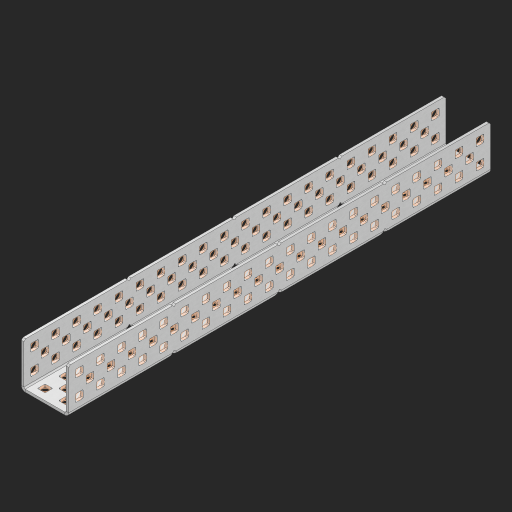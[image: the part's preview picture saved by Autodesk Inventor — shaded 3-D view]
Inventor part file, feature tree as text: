
AUTODESK INVENTOR PART (.ipt)
format: ipt  version: 2023 (Build 270158000, 158)  size: 2,158,080 bytes
history: native  units: in
note: dims shown in document units (in); Inventor stores cm internally (conversion verified against a paired STEP export)
features: other x263, extrude x234, sheet_metal_op x8, sketch x7, mirror x3, pattern_linear x2, chamfer x1
ambient origin geometry x8: Origin, YZ Plane, XZ Plane, XY Plane, X Axis, Y Axis, Z Axis, Center Point
bodies: Solid1 (feature_tree), Body (feature_tree)
feature tree (518):
  other  "Table"
  other  "Alu C 1x2x1x20"
  other  "Alu C 1x2x1x19"
  other  "Alu C 1x2x1x18"
  other  "Alu C 1x2x1x17"
  other  "Alu C 1x2x1x16"
  other  "Alu C 1x2x1x15"
  other  "Alu C 1x2x1x14"
  other  "Alu C 1x2x1x13"
  other  "Alu C 1x2x1x12"
  other  "Alu C 1x2x1x11"
  other  "Alu C 1x2x1x10"
  other  "Alu C 1x2x1x9"
  other  "Alu C 1x2x1x8"
  other  "Alu C 1x2x1x7"
  other  "Alu C 1x2x1x6"
  other  "Alu C 1x2x1x5"
  other  "Alu C 1x2x1x4"
  other  "Alu C 1x2x1x3"
  other  "Alu C 1x2x1x2"
  other  "Alu C 1x2x1x1"
  sheet_metal_op  "Flanges"
  sheet_metal_op  "Body Pattern"
  pattern_linear  "Center Pattern"  Spacing1=1.0in  [1 undecoded]
  other  "Arc Length"
  mirror  "Notch Mirror"
  pattern_linear  "Notch Pattern"  Spacing1=0.25in  [1 undecoded]
  other  "Diagonal Plane"
  mirror  "Flange 1"
  mirror  "Flange 2"
  chamfer  "End Chamfer"
  sketch  "Sketch1"  dims[d0=1.0in]
  other  "Plate1"
  sketch  "Sketch2"  dims[d1=10.0in]
  other  "Plate2"
  sheet_metal_op  "Bend1"
  sheet_metal_op  "Corner1"
  sketch  "Sketch8"  dims[d2=0.0625in]
  sketch  "Sketch9"  dims[d3=0.0625in]
  other  "Srf91"
  sheet_metal_op  "Body Pattern Sketch"
  other  "Srf92"
  sketch  "Sketch13"  dims[d4=0.0312in]
  sketch  "Sketch15"  dims[d5=0.125in]
  sketch  "Sketch16"  dims[d6=0.0625in d7=1.0in d8=90.0deg d9=0.0312in d10=0.25in d11=0.0625in d12=0.0625in d49=0.182in d50=0.02in d52=0.25in d53=0.0625in d54=0.0in d55=0.172in d56=1.0in d57=0.0in d60=7.874in d62=0.5in d63=0.7874in d65=0.5in d85=0.1473in d86=0.1782in d88=0.04in d89=0.0625in d90=0.0in d91=0.04in d92=0.0491in d95=2.5in d96=0.04in d97=0.25in d98=45.0deg d99=0.25in d102=2.497in d106=0.182in d107=0.02in d108=0.5in d110=0.0625in d111=0.0in d112=0.172in d113=0.5in d114=0.0in d117=0.5in d118=0.5in d131=0.25in d132=0.25in]
  other  "Srf786"
  other  "Srf889"
  other  "Srf890"
  other  "Srf891"
  other  "Srf892"
  other  "Srf893"
  other  "Srf894"
  other  "Srf895"
  other  "Srf896"
  other  "Srf996"
  other  "Srf997"
  other  "Srf998"
  other  "Srf999"
  other  "Srf1000"
  other  "Srf1255"
  other  "Srf1256"
  other  "Srf1257"
  other  "Srf1258"
  other  "Srf1259"
  other  "Srf1315"
  other  "Srf1316"
  other  "Srf1317"
  other  "Srf1325"
  other  "Srf1326"
  other  "Srf1327"
  other  "Srf1328"
  other  "Srf1329"
  other  "Srf1330"
  other  "Srf1331"
  other  "Srf1332"
  other  "Srf1338"
  other  "Srf1339"
  other  "Srf1340"
  other  "Srf1341"
  other  "Srf1342"
  other  "Srf1369"
  other  "Srf1370"
  other  "Srf1371"
  other  "Srf1372"
  other  "Srf1373"
  other  "Srf1374"
  other  "Srf1375"
  other  "Srf1376"
  other  "Srf1384"
  other  "Srf1385"
  other  "Srf1386"
  other  "Srf1387"
  other  "Srf1388"
  other  "Srf1389"
  other  "Srf1390"
  other  "Srf1391"
  other  "Srf1397"
  other  "Srf1398"
  other  "Srf1399"
  other  "Srf1400"
  other  "Srf1401"
  other  "Srf1428"
  other  "Srf1429"
  other  "Srf1430"
  other  "Srf1431"
  other  "Srf1432"
  other  "Srf1433"
  other  "Srf1434"
  other  "Srf1473"
  other  "Srf1474"
  other  "Srf1475"
  other  "Srf1476"
  other  "Srf1477"
  other  "Srf1478"
  other  "Srf1479"
  other  "Srf1480"
  other  "Srf1481"
  other  "Srf1482"
  other  "Srf1483"
  other  "Srf1484"
  other  "Srf1485"
  other  "Srf1486"
  other  "Srf1487"
  other  "Srf1488"
  other  "Srf1489"
  other  "Srf1490"
  other  "Srf1491"
  other  "Srf1500"
  other  "Srf1501"
  other  "Srf1502"
  other  "Srf1503"
  other  "Srf1504"
  other  "Srf1505"
  other  "Srf1506"
  other  "Srf1507"
  other  "Srf1508"
  other  "Srf1509"
  other  "Srf1510"
  other  "Srf1511"
  other  "Srf1512"
  other  "Srf1513"
  other  "Srf1514"
  other  "Srf1515"
  other  "Srf1516"
  other  "Srf1517"
  other  "Srf1518"
  other  "Srf1519"
  other  "Srf1520"
  other  "Srf1521"
  other  "Srf1522"
  other  "Srf1523"
  other  "Srf1524"
  other  "Srf1525"
  other  "Srf1526"
  other  "Srf1527"
  other  "Srf1528"
  other  "Srf1529"
  other  "Srf1530"
  other  "Srf1531"
  other  "Srf1532"
  other  "Srf1533"
  other  "Srf1534"
  other  "Srf1535"
  other  "Srf1536"
  other  "Srf1537"
  other  "Srf1538"
  other  "Srf1539"
  other  "Srf1540"
  other  "Srf1541"
  other  "Srf1542"
  other  "Srf1543"
  other  "Srf1544"
  other  "Srf1545"
  other  "Srf1546"
  other  "Srf1547"
  other  "Srf1548"
  other  "Srf1549"
  other  "Srf1550"
  other  "Srf1551"
  other  "Srf1552"
  other  "Srf1553"
  other  "Srf1554"
  other  "Srf1555"
  other  "Srf1556"
  other  "Srf1557"
  other  "Srf1558"
  other  "Srf1559"
  other  "Srf1560"
  other  "Srf1561"
  other  "Srf1562"
  other  "Srf1563"
  other  "Srf1564"
  other  "Srf1565"
  other  "Srf1566"
  other  "Srf1567"
  other  "Srf1568"
  other  "Srf1569"
  other  "Srf1570"
  other  "Srf1571"
  other  "Srf1572"
  other  "Srf1573"
  other  "Srf1574"
  other  "Srf1575"
  other  "Srf1576"
  other  "Srf1577"
  other  "Srf1578"
  other  "Srf1579"
  other  "Srf1580"
  other  "Srf1581"
  other  "Srf1582"
  other  "Srf1583"
  other  "Srf1584"
  other  "Srf1585"
  other  "Srf1586"
  other  "Srf1587"
  other  "Srf1588"
  other  "Srf1589"
  other  "Srf1590"
  other  "Srf1591"
  other  "Srf1592"
  other  "Srf1593"
  other  "Srf1594"
  other  "Srf1595"
  other  "Srf1596"
  other  "Srf1597"
  other  "Srf1598"
  other  "Srf1599"
  other  "Srf1600"
  other  "Srf1601"
  other  "Srf1602"
  other  "Srf1603"
  other  "Srf1604"
  other  "Srf1605"
  other  "Srf1606"
  other  "Srf1607"
  other  "Srf1608"
  other  "Srf1609"
  other  "Srf1610"
  other  "Srf1611"
  other  "Srf1612"
  other  "Srf1613"
  other  "Srf1614"
  other  "Srf1615"
  other  "Srf1616"
  other  "Srf1617"
  other  "Srf1618"
  other  "Srf1619"
  other  "Srf1620"
  other  "Srf1621"
  other  "Srf1622"
  other  "Srf1623"
  other  "Srf1624"
  other  "Srf1625"
  other  "Srf1626"
  other  "Srf1627"
  other  "Srf1628"
  other  "Srf1629"
  other  "Srf1630"
  other  "Srf1631"
  other  "Srf1632"
  other  "Srf1633"
  other  "Srf1634"
  other  "Srf1635"
  other  "Srf1636"
  other  "Srf1637"
  other  "Srf1638"
  other  "Srf1639"
  other  "Srf1640"
  other  "Srf1641"
  other  "Srf1642"
  other  "Srf1643"
  other  "Srf1644"
  other  "Srf1645"
  other  "Srf1646"
  other  "Srf1647"
  other  "Srf1648"
  other  "Srf1649"
  other  "Srf1650"
  other  "Srf1651"
  sheet_metal_op  "Body Stamp"
  sheet_metal_op  "Body Circle"
  other  "Center Stamp"
  other  "Center Circle"
  sheet_metal_op  "Notch"
  extrude  "ExtrusionSrf92"  Depth=0.0625in
  extrude  "ExtrusionSrf889"  Depth=0.0625in
  extrude  "ExtrusionSrf890"  Depth=0.5in
  extrude  "ExtrusionSrf891"  Depth=0.02in
  extrude  "ExtrusionSrf892"  Depth=0.5in
  extrude  "ExtrusionSrf893"  Depth=0.0625in
  extrude  "ExtrusionSrf894"  TaperAngle=0.0deg  [1 undecoded]
  extrude  "ExtrusionSrf895"  Depth=0.5in
  extrude  "ExtrusionSrf896"  Depth=1.0in TaperAngle=0.0deg
  extrude  "ExtrusionSrf996"  Depth=0.5in
  extrude  "ExtrusionSrf997"  Depth=0.5in
  extrude  "ExtrusionSrf998"  Depth=0.5in
  extrude  "ExtrusionSrf999"  Depth=0.5in
  extrude  "ExtrusionSrf1000"  Depth=0.5in
  extrude  "ExtrusionSrf1255"  Depth=0.0625in
  extrude  "ExtrusionSrf1256"  TaperAngle=0.0deg  [1 undecoded]
  extrude  "ExtrusionSrf1257"  Depth=0.5in
  extrude  "ExtrusionSrf1258"  Depth=0.5in
  extrude  "ExtrusionSrf1259"  Depth=2.5in
  extrude  "ExtrusionSrf1315"  Depth=0.5in TaperAngle=45.0deg
  extrude  "ExtrusionSrf1316"  Depth=0.5in
  extrude  "ExtrusionSrf1355"  Depth=0.5in
  extrude  "ExtrusionSrf1356"  Depth=0.5in
  extrude  "ExtrusionSrf1357"  Depth=0.02in
  extrude  "ExtrusionSrf1358"  Depth=0.5in
  extrude  "ExtrusionSrf1359"  Depth=0.0625in
  extrude  "ExtrusionSrf1360"  TaperAngle=0.0deg  [1 undecoded]
  extrude  "ExtrusionSrf1361"  Depth=0.5in
  extrude  "ExtrusionSrf1362"  Depth=0.5in TaperAngle=0.0deg
  extrude  "ExtrusionSrf1363"  Depth=0.5in
  extrude  "ExtrusionSrf1364"  Depth=0.5in
  extrude  "ExtrusionSrf1365"  Depth=0.5in
  extrude  "ExtrusionSrf1366"  Depth=0.5in
  extrude  "ExtrusionSrf1367"  [1 undecoded]
  extrude  "ExtrusionSrf1368"  [1 undecoded]
  extrude  "ExtrusionSrf1369"  [1 undecoded]
  extrude  "ExtrusionSrf1370"  [1 undecoded]
  extrude  "ExtrusionSrf1371"  [1 undecoded]
  extrude  "ExtrusionSrf1372"  [1 undecoded]
  extrude  "ExtrusionSrf1373"  [1 undecoded]
  extrude  "ExtrusionSrf1374"  [1 undecoded]
  extrude  "ExtrusionSrf1375"  [1 undecoded]
  extrude  "ExtrusionSrf1414"  [1 undecoded]
  extrude  "ExtrusionSrf1415"  [1 undecoded]
  extrude  "ExtrusionSrf1416"  [1 undecoded]
  extrude  "ExtrusionSrf1417"  [1 undecoded]
  extrude  "ExtrusionSrf1418"  [1 undecoded]
  extrude  "ExtrusionSrf1419"  [1 undecoded]
  extrude  "ExtrusionSrf1420"  [1 undecoded]
  extrude  "ExtrusionSrf1421"  [1 undecoded]
  extrude  "ExtrusionSrf1422"  [1 undecoded]
  extrude  "ExtrusionSrf1423"  [1 undecoded]
  extrude  "ExtrusionSrf1424"  [1 undecoded]
  extrude  "ExtrusionSrf1425"  [1 undecoded]
  extrude  "ExtrusionSrf1426"  [1 undecoded]
  extrude  "ExtrusionSrf1427"  [1 undecoded]
  extrude  "ExtrusionSrf1428"  [1 undecoded]
  extrude  "ExtrusionSrf1429"  [1 undecoded]
  extrude  "ExtrusionSrf1430"  [1 undecoded]
  extrude  "ExtrusionSrf1431"  [1 undecoded]
  extrude  "ExtrusionSrf1432"  [1 undecoded]
  extrude  "ExtrusionSrf1433"  [1 undecoded]
  extrude  "ExtrusionSrf1434"  [1 undecoded]
  extrude  "ExtrusionSrf1473"  [1 undecoded]
  extrude  "ExtrusionSrf1474"  [1 undecoded]
  extrude  "ExtrusionSrf1475"  [1 undecoded]
  extrude  "ExtrusionSrf1476"  [1 undecoded]
  extrude  "ExtrusionSrf1477"  [1 undecoded]
  extrude  "ExtrusionSrf1478"  [1 undecoded]
  extrude  "ExtrusionSrf1479"  [1 undecoded]
  extrude  "ExtrusionSrf1480"  [1 undecoded]
  extrude  "ExtrusionSrf1481"  [1 undecoded]
  extrude  "ExtrusionSrf1482"  [1 undecoded]
  extrude  "ExtrusionSrf1483"  [1 undecoded]
  extrude  "ExtrusionSrf1484"  [1 undecoded]
  extrude  "ExtrusionSrf1485"  [1 undecoded]
  extrude  "ExtrusionSrf1486"  [1 undecoded]
  extrude  "ExtrusionSrf1487"  [1 undecoded]
  extrude  "ExtrusionSrf1488"  [1 undecoded]
  extrude  "ExtrusionSrf1489"  [1 undecoded]
  extrude  "ExtrusionSrf1490"  [1 undecoded]
  extrude  "ExtrusionSrf1491"  [1 undecoded]
  extrude  "ExtrusionSrf1500"  [1 undecoded]
  extrude  "ExtrusionSrf1501"  [1 undecoded]
  extrude  "ExtrusionSrf1502"  [1 undecoded]
  extrude  "ExtrusionSrf1503"  [1 undecoded]
  extrude  "ExtrusionSrf1504"  [1 undecoded]
  extrude  "ExtrusionSrf1505"  [1 undecoded]
  extrude  "ExtrusionSrf1506"  [1 undecoded]
  extrude  "ExtrusionSrf1507"  [1 undecoded]
  extrude  "ExtrusionSrf1508"  [1 undecoded]
  extrude  "ExtrusionSrf1509"  [1 undecoded]
  extrude  "ExtrusionSrf1510"  [1 undecoded]
  extrude  "ExtrusionSrf1511"  [1 undecoded]
  extrude  "ExtrusionSrf1512"  [1 undecoded]
  extrude  "ExtrusionSrf1513"  [1 undecoded]
  extrude  "ExtrusionSrf1514"  [1 undecoded]
  extrude  "ExtrusionSrf1515"  [1 undecoded]
  extrude  "ExtrusionSrf1516"  [1 undecoded]
  extrude  "ExtrusionSrf1517"  [1 undecoded]
  extrude  "ExtrusionSrf1518"  [1 undecoded]
  extrude  "ExtrusionSrf1519"  [1 undecoded]
  extrude  "ExtrusionSrf1520"  [1 undecoded]
  extrude  "ExtrusionSrf1521"  [1 undecoded]
  extrude  "ExtrusionSrf1522"  [1 undecoded]
  extrude  "ExtrusionSrf1523"  [1 undecoded]
  extrude  "ExtrusionSrf1524"  [1 undecoded]
  extrude  "ExtrusionSrf1525"  [1 undecoded]
  extrude  "ExtrusionSrf1526"  [1 undecoded]
  extrude  "ExtrusionSrf1527"  [1 undecoded]
  extrude  "ExtrusionSrf1528"  [1 undecoded]
  extrude  "ExtrusionSrf1529"  [1 undecoded]
  extrude  "ExtrusionSrf1530"  [1 undecoded]
  extrude  "ExtrusionSrf1531"  [1 undecoded]
  extrude  "ExtrusionSrf1532"  [1 undecoded]
  extrude  "ExtrusionSrf1533"  [1 undecoded]
  extrude  "ExtrusionSrf1534"  [1 undecoded]
  extrude  "ExtrusionSrf1535"  [1 undecoded]
  extrude  "ExtrusionSrf1536"  [1 undecoded]
  extrude  "ExtrusionSrf1537"  [1 undecoded]
  extrude  "ExtrusionSrf1538"  [1 undecoded]
  extrude  "ExtrusionSrf1539"  [1 undecoded]
  extrude  "ExtrusionSrf1540"  [1 undecoded]
  extrude  "ExtrusionSrf1541"  [1 undecoded]
  extrude  "ExtrusionSrf1542"  [1 undecoded]
  extrude  "ExtrusionSrf1543"  [1 undecoded]
  extrude  "ExtrusionSrf1544"  [1 undecoded]
  extrude  "ExtrusionSrf1545"  [1 undecoded]
  extrude  "ExtrusionSrf1546"  [1 undecoded]
  extrude  "ExtrusionSrf1547"  [1 undecoded]
  extrude  "ExtrusionSrf1548"  [1 undecoded]
  extrude  "ExtrusionSrf1549"  [1 undecoded]
  extrude  "ExtrusionSrf1550"  [1 undecoded]
  extrude  "ExtrusionSrf1551"  [1 undecoded]
  extrude  "ExtrusionSrf1552"  [1 undecoded]
  extrude  "ExtrusionSrf1553"  [1 undecoded]
  extrude  "ExtrusionSrf1554"  [1 undecoded]
  extrude  "ExtrusionSrf1555"  [1 undecoded]
  extrude  "ExtrusionSrf1556"  [1 undecoded]
  extrude  "ExtrusionSrf1557"  [1 undecoded]
  extrude  "ExtrusionSrf1558"  [1 undecoded]
  extrude  "ExtrusionSrf1559"  [1 undecoded]
  extrude  "ExtrusionSrf1560"  [1 undecoded]
  extrude  "ExtrusionSrf1561"  [1 undecoded]
  extrude  "ExtrusionSrf1562"  [1 undecoded]
  extrude  "ExtrusionSrf1563"  [1 undecoded]
  extrude  "ExtrusionSrf1564"  [1 undecoded]
  extrude  "ExtrusionSrf1565"  [1 undecoded]
  extrude  "ExtrusionSrf1566"  [1 undecoded]
  extrude  "ExtrusionSrf1567"  [1 undecoded]
  extrude  "ExtrusionSrf1568"  [1 undecoded]
  extrude  "ExtrusionSrf1569"  [1 undecoded]
  extrude  "ExtrusionSrf1570"  [1 undecoded]
  extrude  "ExtrusionSrf1571"  [1 undecoded]
  extrude  "ExtrusionSrf1572"  [1 undecoded]
  extrude  "ExtrusionSrf1573"  [1 undecoded]
  extrude  "ExtrusionSrf1574"  [1 undecoded]
  extrude  "ExtrusionSrf1575"  [1 undecoded]
  extrude  "ExtrusionSrf1576"  [1 undecoded]
  extrude  "ExtrusionSrf1577"  [1 undecoded]
  extrude  "ExtrusionSrf1578"  [1 undecoded]
  extrude  "ExtrusionSrf1579"  [1 undecoded]
  extrude  "ExtrusionSrf1580"  [1 undecoded]
  extrude  "ExtrusionSrf1581"  [1 undecoded]
  extrude  "ExtrusionSrf1582"  [1 undecoded]
  extrude  "ExtrusionSrf1583"  [1 undecoded]
  extrude  "ExtrusionSrf1584"  [1 undecoded]
  extrude  "ExtrusionSrf1585"  [1 undecoded]
  extrude  "ExtrusionSrf1586"  [1 undecoded]
  extrude  "ExtrusionSrf1587"  [1 undecoded]
  extrude  "ExtrusionSrf1588"  [1 undecoded]
  extrude  "ExtrusionSrf1589"  [1 undecoded]
  extrude  "ExtrusionSrf1590"  [1 undecoded]
  extrude  "ExtrusionSrf1591"  [1 undecoded]
  extrude  "ExtrusionSrf1592"  [1 undecoded]
  extrude  "ExtrusionSrf1593"  [1 undecoded]
  extrude  "ExtrusionSrf1594"  [1 undecoded]
  extrude  "ExtrusionSrf1595"  [1 undecoded]
  extrude  "ExtrusionSrf1596"  [1 undecoded]
  extrude  "ExtrusionSrf1597"  [1 undecoded]
  extrude  "ExtrusionSrf1598"  [1 undecoded]
  extrude  "ExtrusionSrf1599"  [1 undecoded]
  extrude  "ExtrusionSrf1600"  [1 undecoded]
  extrude  "ExtrusionSrf1601"  [1 undecoded]
  extrude  "ExtrusionSrf1602"  [1 undecoded]
  extrude  "ExtrusionSrf1603"  [1 undecoded]
  extrude  "ExtrusionSrf1604"  [1 undecoded]
  extrude  "ExtrusionSrf1605"  [1 undecoded]
  extrude  "ExtrusionSrf1606"  [1 undecoded]
  extrude  "ExtrusionSrf1607"  [1 undecoded]
  extrude  "ExtrusionSrf1608"  [1 undecoded]
  extrude  "ExtrusionSrf1609"  [1 undecoded]
  extrude  "ExtrusionSrf1610"  [1 undecoded]
  extrude  "ExtrusionSrf1611"  [1 undecoded]
  extrude  "ExtrusionSrf1612"  [1 undecoded]
  extrude  "ExtrusionSrf1613"  [1 undecoded]
  extrude  "ExtrusionSrf1614"  [1 undecoded]
  extrude  "ExtrusionSrf1615"  [1 undecoded]
  extrude  "ExtrusionSrf1616"  [1 undecoded]
  extrude  "ExtrusionSrf1617"  [1 undecoded]
  extrude  "ExtrusionSrf1618"  [1 undecoded]
  extrude  "ExtrusionSrf1619"  [1 undecoded]
  extrude  "ExtrusionSrf1620"  [1 undecoded]
  extrude  "ExtrusionSrf1621"  [1 undecoded]
  extrude  "ExtrusionSrf1622"  [1 undecoded]
  extrude  "ExtrusionSrf1623"  [1 undecoded]
  extrude  "ExtrusionSrf1624"  [1 undecoded]
  extrude  "ExtrusionSrf1625"  [1 undecoded]
  extrude  "ExtrusionSrf1626"  [1 undecoded]
  extrude  "ExtrusionSrf1627"  [1 undecoded]
  extrude  "ExtrusionSrf1628"  [1 undecoded]
  extrude  "ExtrusionSrf1629"  [1 undecoded]
  extrude  "ExtrusionSrf1630"  [1 undecoded]
  extrude  "ExtrusionSrf1631"  [1 undecoded]
  extrude  "ExtrusionSrf1632"  [1 undecoded]
  extrude  "ExtrusionSrf1633"  [1 undecoded]
  extrude  "ExtrusionSrf1634"  [1 undecoded]
  extrude  "ExtrusionSrf1635"  [1 undecoded]
  extrude  "ExtrusionSrf1636"  [1 undecoded]
  extrude  "ExtrusionSrf1637"  [1 undecoded]
  extrude  "ExtrusionSrf1638"  [1 undecoded]
  extrude  "ExtrusionSrf1639"  [1 undecoded]
  extrude  "ExtrusionSrf1640"  [1 undecoded]
  extrude  "ExtrusionSrf1641"  [1 undecoded]
  extrude  "ExtrusionSrf1642"  [1 undecoded]
  extrude  "ExtrusionSrf1643"  [1 undecoded]
  extrude  "ExtrusionSrf1644"  [1 undecoded]
  extrude  "ExtrusionSrf1645"  [1 undecoded]
  extrude  "ExtrusionSrf1646"  [1 undecoded]
  extrude  "ExtrusionSrf1647"  [1 undecoded]
  extrude  "ExtrusionSrf1648"  [1 undecoded]
  extrude  "ExtrusionSrf1649"  [1 undecoded]
  extrude  "ExtrusionSrf1650"  [1 undecoded]
  extrude  "ExtrusionSrf1651"  [1 undecoded]
note: 206 required parameter values undecoded (feature->parameter linkage not recoverable at this tier; creation-order binding heuristic only, values carry confidence <= 0.55)
